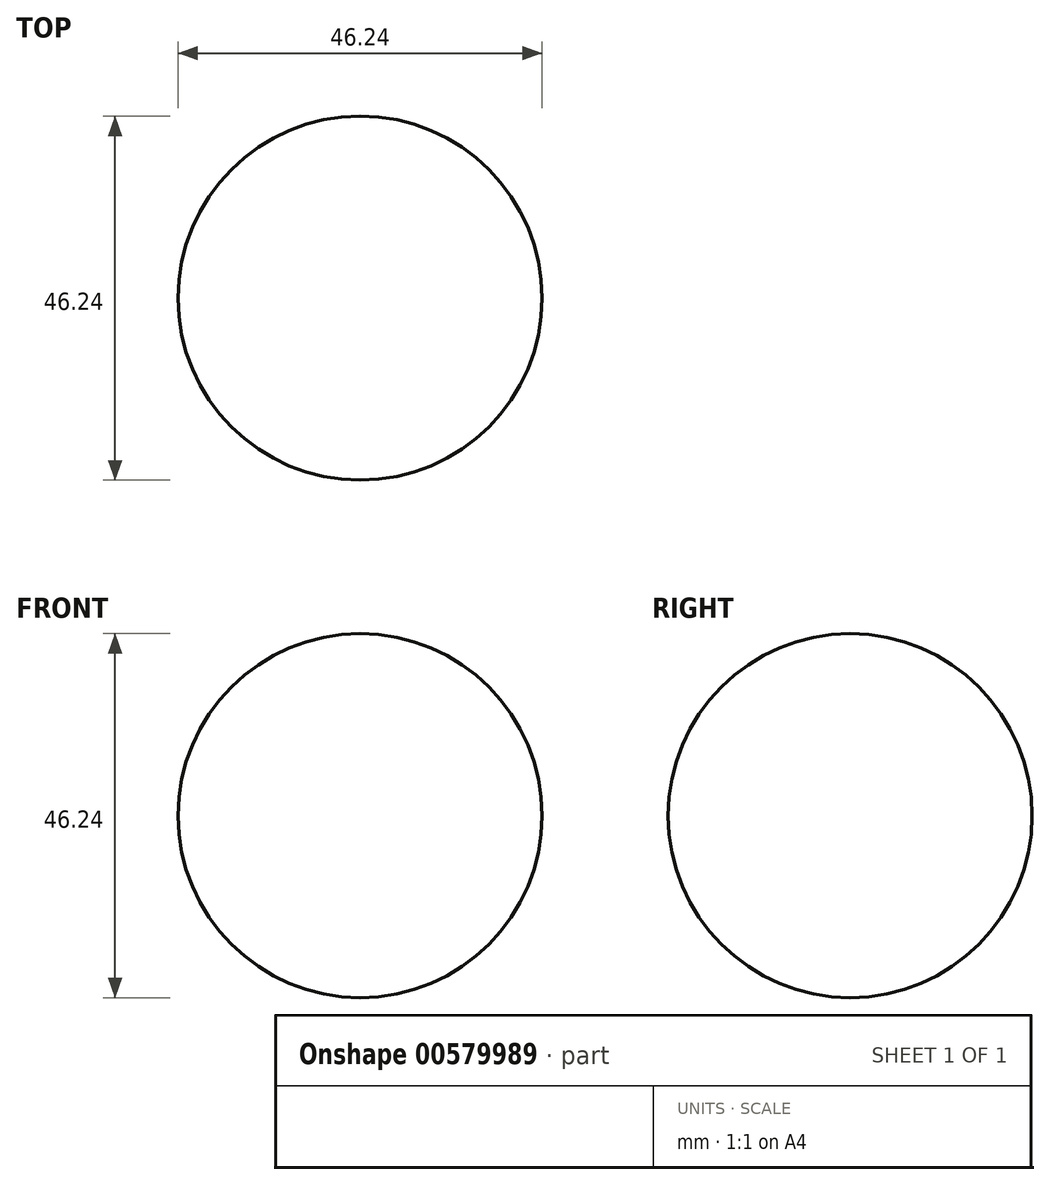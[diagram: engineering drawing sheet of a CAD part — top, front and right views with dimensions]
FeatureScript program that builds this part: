
annotation { "Feature Type Name" : "Feature", "Feature Type Description" : "" }
export const myFeature = defineFeature(function(context is Context, id is Id, definition is map)
    precondition{}
    {
        {
            var Q0;
            Q0=qCreatedBy(makeId("Front.planeOp"),FACE);
            var sketch = newSketch(context, id + "F0", { "sketchPlane" : qUnion([Q0])});
            skArc(sketch, "E0", {"start": v(23.12, 0) * mm, "mid": v(0, 23.12) * mm, "end": v(-23.12, 0) * mm});
            skLineSegment(sketch, "E1", {"start": v(23.12, 0) * mm, "end": v(-23.12, 0) * mm});
            skLineSegment(sketch, "E2", {"start": v(0, 0) * mm, "end": v(0, 23.12) * mm});
            skSolve(sketch);
        }
        {
            var Q0;
            {var subQ3=sQuery(id+"F0.wireOp",EDGE,"E2");Q0=makeQuery(id+"F0.imprint","IMPRINT",FACE,{"disambiguationData":[TD([[makeQuery(id+"F0.imprint","IMPRINT",EDGE,{"derivedFrom":subQ3}),-1.0]])]});}
            var Q1;
            {var subQ3=sQuery(id+"F0.wireOp",EDGE,"E2");Q1=makeQuery(id+"F0.imprint","IMPRINT",FACE,{"disambiguationData":[TD([[makeQuery(id+"F0.imprint","IMPRINT",EDGE,{"derivedFrom":subQ3}),1.0]])]});}
            var Q2;
            Q2=sQuery(id+"F0.wireOp",EDGE,"E1");
            revolve(context, id + "F1", {"entities" : qUnion([Q0, Q1]), "axis" : qUnion([Q2]), "revolveType" : RevolveType.FULL});
        }
    });
